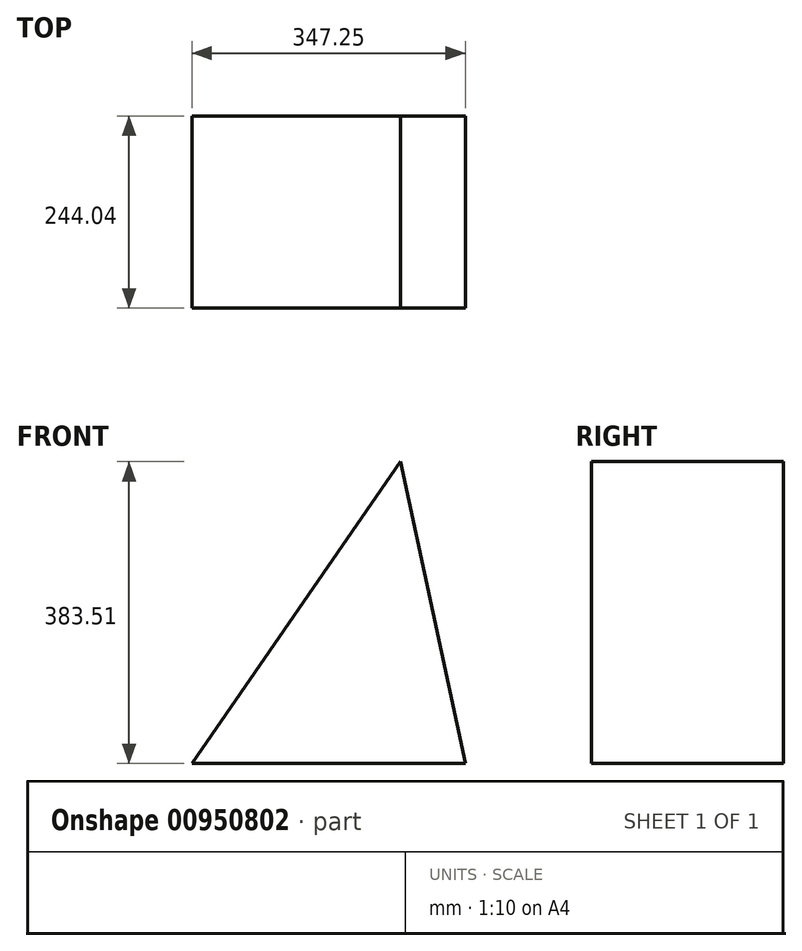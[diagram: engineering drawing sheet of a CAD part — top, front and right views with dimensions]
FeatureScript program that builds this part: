
annotation { "Feature Type Name" : "Feature", "Feature Type Description" : "" }
export const myFeature = defineFeature(function(context is Context, id is Id, definition is map)
    precondition{}
    {
        {
            var Q0;
            Q0=qCreatedBy(makeId("Front.planeOp"),FACE);
            var sketch = newSketch(context, id + "F0", { "sketchPlane" : qUnion([Q0])});
            skLineSegment(sketch, "E0", {"start": v(-159.97, -43.58) * mm, "end": v(-159.97, 56.4) * mm});
            skLineSegment(sketch, "E1", {"start": v(-159.97, 56.4) * mm, "end": v(-343.7, -6.45) * mm});
            skLineSegment(sketch, "E2", {"start": v(-343.7, -6.45) * mm, "end": v(-190.36, -50.1) * mm});
            skLineSegment(sketch, "E3", {"start": v(-190.36, -50.1) * mm, "end": v(-238.01, -50.1) * mm});
            skLineSegment(sketch, "E4", {"start": v(-238.01, -50.1) * mm, "end": v(-218.65, -104.62) * mm});
            skLineSegment(sketch, "E5", {"start": v(-218.65, -104.62) * mm, "end": v(-159.97, -43.58) * mm});
            skLineSegment(sketch, "E6", {"start": v(-318.04, 121.36) * mm, "end": v(-343.7, -6.45) * mm});
            skLineSegment(sketch, "E7", {"start": v(-159.97, 56.4) * mm, "end": v(-318.04, 121.36) * mm});
            skLineSegment(sketch, "E8", {"start": v(-255.26, -86.08) * mm, "end": v(-238.01, -50.1) * mm});
            skLineSegment(sketch, "E9", {"start": v(-218.65, -104.62) * mm, "end": v(-255.26, -86.08) * mm});
            skCircle(sketch, "E10", {"center": v(-391.83, 44.87) * mm, "radius": 55.63 * mm});
            skArc(sketch, "E11", {"start": v(-318.04, 121.36) * mm, "mid": v(-481.67, 179.28) * mm, "end": v(-645.3, 121.36) * mm});
            skArc(sketch, "E12", {"start": v(-645.3, 121.36) * mm, "mid": v(-622.5, -27.5) * mm, "end": v(-481.67, -80.78) * mm});
            skLineSegment(sketch, "E13", {"start": v(-343.7, -6.45) * mm, "end": v(-481.67, -80.78) * mm});
            skLineSegment(sketch, "E14", {"start": v(-1340.26, 474.41) * mm, "end": v(-1340.26, 474.41) * mm});
            skLineSegment(sketch, "E15", {"start": v(-834.16, 189.2) * mm, "end": v(-752.06, -194.3) * mm});
            skLineSegment(sketch, "E16", {"start": v(-752.06, -194.3) * mm, "end": v(-1099.3, -194.3) * mm});
            skLineSegment(sketch, "E17", {"start": v(-834.16, 189.2) * mm, "end": v(-1099.3, -194.3) * mm});
            skLineSegment(sketch, "E18", {"start": v(-1124.9, 238.7) * mm, "end": v(-973.84, 238.7) * mm});
            skLineSegment(sketch, "E19", {"start": v(-1124.9, 238.7) * mm, "end": v(-1099.3, -194.3) * mm});
            skLineSegment(sketch, "E20", {"start": v(-973.84, 238.7) * mm, "end": v(-834.16, 189.2) * mm});
            skSolve(sketch);
        }
        {
            var Q0;
            Q0=makeQuery(id+"F0.imprint","IMPRINT",FACE,{"disambiguationData":[TD([[makeQuery(id+"F0.imprint","IMPRINT",EDGE,{"derivedFrom":sQuery(id+"F0.wireOp",EDGE,"E15")}),-1.0]])]});
            extrude(context, id + "F1", {"entities" : qUnion([Q0]), "depth" : 244.04 * mm, "offsetDistance" : 25 * mm});
        }
    });
